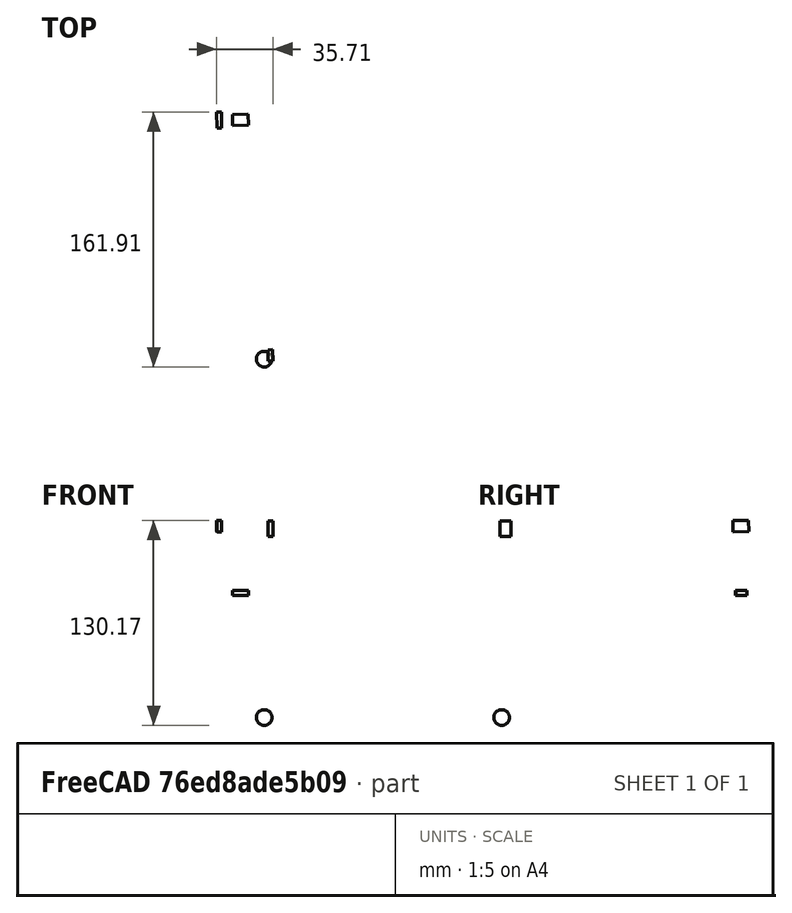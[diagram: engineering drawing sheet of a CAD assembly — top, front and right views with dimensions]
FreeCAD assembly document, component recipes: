
FREECAD ASSEMBLY — COMPONENT RECIPES ("3axis_robot_forced_reduced")

This assembly document has 3 components, labeled P0..P2 below (a component is one placed body or linked part). 3 of them carry a construction recipe — the FreeCAD feature program that regenerates the part from scratch, quoted from this document or its linked companion documents; the rest are supplied as boundary geometry only. No exploded tour is included for this assembly.
COMPONENT P0 — recipe-attached ("arm0", a linked part whose construction recipe lives in a companion FreeCAD document of the same project; that document's serialized recipe follows).
Construction recipe (the companion document, serialized — sketch geometry with constraints, then the solid features built on it; lengths are millimeters unless a unit is written):

FCSTD DOCUMENT  (FreeCAD 2024.1R35694 (Git))
Label: arm0
License: All rights reserved
LicenseURL: https://en.wikipedia.org/wiki/All_rights_reserved
objects: Sketcher::SketchObject×11, PartDesign::Pad×6, PartDesign::Hole×3, PartDesign::Body×2, PartDesign::Pocket×2, PartDesign::Fillet×1, App::Part×1
note: 37 computed .brp shape members not serialized (recipe doc carries the construction recipe); baked Part::Feature solids carry a one-line shape summary decoded from their .brp

FEATURE [Sketcher::SketchObject] Sketch
  FullyConstrained = true
  MapMode = 5
  Support = -> [XY_Plane001]
  sketch-geometry (5):
    g0: Circle CenterX=0 CenterY=0 CenterZ=0 NormalX=0 NormalY=0 NormalZ=1 AngleXU=0 Radius=2.5
    g1: ArcOfCircle CenterX=0 CenterY=0 CenterZ=0 NormalX=0 NormalY=0 NormalZ=1 AngleXU=0 Radius=7.5 StartAngle=1.5708 EndAngle=4.71239
    g2: LineSegment StartX=-1.2e-15 StartY=7.5 StartZ=0 EndX=15 EndY=7.5 EndZ=0
    g3: LineSegment StartX=15 StartY=7.5 StartZ=0 EndX=15 EndY=-7.5 EndZ=0
    g4: LineSegment StartX=15 StartY=-7.5 StartZ=0 EndX=1.8e-15 EndY=-7.5 EndZ=0
  constraints (12):
    c: Coincident(g0,g-1)
    c: Coincident(g1,g0)
    c: Diameter(g0) = 5
    c: Diameter(g1) = 15
    c: Horizontal(g2)
    c: Coincident(g2,g3)
    c: Vertical(g3)
    c: Coincident(g3,g4)
    c: Horizontal(g4)
    c: Tangent(g1,g4) = 1.5708
    c: Tangent(g1,g2) = 1.5708
    c: DistanceX(g2,g2) = 15
FEATURE [PartDesign::Pad] Pad
  Direction = (0,0,1)
  Length = 20
  Length2 = 10
  Profile = -> Sketch
  ReferenceAxis = -> Sketch [N_Axis]
  Refine = true
  Type = 0
FEATURE [Sketcher::SketchObject] Sketch001
  ExternalGeometry = -> [Pad]
  FullyConstrained = true
  MapMode = 5
  Placement = pos=(15,0,0) rot=(0.57735,0.57735,0.57735;2.0944rad)
  Support = -> [Pad]
  sketch-geometry (8):
    g0: LineSegment StartX=-7.5 StartY=0 StartZ=0 EndX=-21 EndY=43 EndZ=0
    g1: LineSegment StartX=-21 StartY=43 StartZ=0 EndX=-21 EndY=85 EndZ=0
    g2: LineSegment StartX=-21 StartY=85 StartZ=0 EndX=21 EndY=85 EndZ=0
    g3: LineSegment StartX=21 StartY=85 StartZ=0 EndX=21 EndY=43 EndZ=0
    g4: LineSegment StartX=21 StartY=43 StartZ=0 EndX=7.5 EndY=0 EndZ=0
    g5: LineSegment StartX=7.5 StartY=0 StartZ=0 EndX=-7.5 EndY=0 EndZ=0
    g6: GeomPoint X=5.2e-15 Y=64 Z=0
    g7: Circle CenterX=5.2e-15 CenterY=64 CenterZ=0 NormalX=0 NormalY=0 NormalZ=1 AngleXU=0 Radius=11.25
  constraints (18):
    c: PointOnObject(g0,g-1)
    c: Coincident(g0,g1)
    c: Vertical(g1)
    c: Coincident(g1,g2)
    c: Coincident(g2,g3)
    c: Coincident(g3,g4)
    c: Coincident(g4,g5)
    c: Coincident(g5,g0)
    c: Symmetric(g0,g3,g-2)
    c: Symmetric(g1,g2,g-2)
    c: DistanceX(g2,g2) = 42
    c: DistanceY(g3,g3) = 42
    c: Symmetric(g0,g4,g-2)
    c: DistanceX(g5,g5) = 15
    c: Symmetric(g1,g3,g6)
    c: Coincident(g7,g6)
    c: Diameter(g7) = 22.5
    c: DistanceY(g-1,g3) = 43
FEATURE [PartDesign::Pad] Pad001
  BaseFeature = -> Pad
  Direction = (1,0,0)
  Length = 4
  Length2 = 10
  Profile = -> Sketch001
  ReferenceAxis = -> Sketch001 [N_Axis]
  Refine = true
  Reversed = true
  Type = 0
FEATURE [Sketcher::SketchObject] Sketch003
  ExternalGeometry = -> [Pad001]
  FullyConstrained = true
  MapMode = 5
  Placement = pos=(11,0,0) rot=(0.57735,-0.57735,-0.57735;2.0944rad)
  Support = -> [Pad001]
  sketch-geometry (5):
    g0: Circle CenterX=15.5 CenterY=79.5 CenterZ=0 NormalX=0 NormalY=0 NormalZ=1 AngleXU=0 Radius=1.5
    g1: LineSegment StartX=-5.2e-15 StartY=64 StartZ=0 EndX=11.25 EndY=64 EndZ=0
    g2: Circle CenterX=-15.5 CenterY=79.5 CenterZ=0 NormalX=0 NormalY=0 NormalZ=1 AngleXU=0 Radius=1.5
    g3: Circle CenterX=15.5 CenterY=48.5 CenterZ=0 NormalX=0 NormalY=0 NormalZ=1 AngleXU=0 Radius=1.5
    g4: Circle CenterX=-15.5 CenterY=48.5 CenterZ=0 NormalX=0 NormalY=0 NormalZ=1 AngleXU=0 Radius=1.5
  constraints (12):
    c: DistanceY(g-3,g0) = 15.5
    c: DistanceX(g-3,g0) = 15.5
    c: Diameter(g0) = 3
    c: Coincident(g1,g-3)
    c: Horizontal(g1)
    c: PointOnObject(g1,g-3)
    c: Diameter(g2) = 3
    c: Diameter(g3) = 3
    c: Diameter(g4) = 3
    c: Symmetric(g2,g0,g-2)
    c: Symmetric(g4,g3,g-2)
    c: Symmetric(g3,g0,g1)
FEATURE [PartDesign::Hole] Hole
  BaseFeature = -> Pad001
  CustomThreadClearance = 0
  Depth = 25
  DepthType = 0
  Diameter = 3.4
  DrillForDepth = false
  DrillPoint = 1
  DrillPointAngle = 118
  HoleCutCountersinkAngle = 90
  HoleCutCustomValues = false
  HoleCutDepth = 2
  HoleCutDiameter = 6.1
  HoleCutType = 1
  ModelThread = false
  Profile = -> Sketch003
  Refine = true
  Tapered = false
  TaperedAngle = 90
  ThreadClass = 0
  ThreadDepth = 25
  ThreadDepthType = 0
  ThreadDirection = 0
  ThreadFit = 0
  ThreadSize = 9
  ThreadType = 1
  Threaded = false
  UseCustomThreadClearance = false
FEATURE [Sketcher::SketchObject] Sketch004
  ExternalGeometry = -> [Hole]
  FullyConstrained = true
  MapMode = 5
  Placement = pos=(0,0,20) rot=(0,0,1;0rad)
  Support = -> [Hole]
  sketch-geometry (1):
    g0: Circle CenterX=0 CenterY=0 CenterZ=0 NormalX=0 NormalY=0 NormalZ=1 AngleXU=0 Radius=2.5
  constraints (2):
    c: Coincident(g0,g-3)
    c: Equal(g0,g-3)
FEATURE [PartDesign::Pad] Pad002
  BaseFeature = -> Hole
  Direction = (0,0,1)
  Length = 2
  Length2 = 10
  Profile = -> Sketch004
  ReferenceAxis = -> Sketch004 [N_Axis]
  Refine = true
  Reversed = true
  Type = 0
FEATURE [PartDesign::Body] Body  label="arm0-skel"
  Group = -> [Sketch,Pad,Sketch001,Pad001,Sketch003,Hole,Sketch004,Pad002]
  Origin = -> Origin001
  Tip = -> Pad002
FEATURE [Sketcher::SketchObject] Sketch008
  FullyConstrained = true
  MapMode = 5
  Support = -> [XY_Plane002]
  sketch-geometry (5):
    g0: Circle CenterX=0 CenterY=0 CenterZ=0 NormalX=0 NormalY=0 NormalZ=1 AngleXU=0 Radius=2.5
    g1: ArcOfCircle CenterX=0 CenterY=0 CenterZ=0 NormalX=0 NormalY=0 NormalZ=1 AngleXU=0 Radius=7.5 StartAngle=1.5708 EndAngle=4.71239
    g2: LineSegment StartX=-1.2e-15 StartY=7.5 StartZ=0 EndX=15 EndY=7.5 EndZ=0
    g3: LineSegment StartX=15 StartY=7.5 StartZ=0 EndX=15 EndY=-7.5 EndZ=0
    g4: LineSegment StartX=15 StartY=-7.5 StartZ=0 EndX=1.8e-15 EndY=-7.5 EndZ=0
  constraints (12):
    c: Coincident(g0,g-1)
    c: Coincident(g1,g0)
    c: Diameter(g0) = 5
    c: Diameter(g1) = 15
    c: Horizontal(g2)
    c: Coincident(g2,g3)
    c: Vertical(g3)
    c: Coincident(g3,g4)
    c: Horizontal(g4)
    c: Tangent(g1,g4) = 1.5708
    c: Tangent(g1,g2) = 1.5708
    c: DistanceX(g2,g2) = 15
FEATURE [PartDesign::Pad] Pad003
  Direction = (0,0,1)
  Length = 20
  Length2 = 10
  Profile = -> Sketch008
  ReferenceAxis = -> Sketch008 [N_Axis]
  Refine = true
  Type = 0
FEATURE [Sketcher::SketchObject] Sketch009
  ExternalGeometry = -> [Pad003]
  FullyConstrained = true
  MapMode = 5
  Placement = pos=(15,0,0) rot=(0.57735,0.57735,0.57735;2.0944rad)
  Support = -> [Pad003]
  sketch-geometry (8):
    g0: LineSegment StartX=-7.5 StartY=0 StartZ=0 EndX=-21 EndY=43 EndZ=0
    g1: LineSegment StartX=-21 StartY=43 StartZ=0 EndX=-21 EndY=85 EndZ=0
    g2: LineSegment StartX=-21 StartY=85 StartZ=0 EndX=21 EndY=85 EndZ=0
    g3: LineSegment StartX=21 StartY=85 StartZ=0 EndX=21 EndY=43 EndZ=0
    g4: LineSegment StartX=21 StartY=43 StartZ=0 EndX=7.5 EndY=0 EndZ=0
    g5: LineSegment StartX=7.5 StartY=0 StartZ=0 EndX=-7.5 EndY=0 EndZ=0
    g6: GeomPoint X=4.8e-15 Y=64 Z=0
    g7: Circle CenterX=4.8e-15 CenterY=64 CenterZ=0 NormalX=0 NormalY=0 NormalZ=1 AngleXU=0 Radius=11.25
  constraints (18):
    c: PointOnObject(g0,g-1)
    c: Coincident(g0,g1)
    c: Vertical(g1)
    c: Coincident(g1,g2)
    c: Coincident(g2,g3)
    c: Coincident(g3,g4)
    c: Coincident(g4,g5)
    c: Coincident(g5,g0)
    c: Symmetric(g0,g3,g-2)
    c: Symmetric(g1,g2,g-2)
    c: DistanceX(g2,g2) = 42
    c: DistanceY(g3,g3) = 42
    c: Symmetric(g0,g4,g-2)
    c: DistanceX(g5,g5) = 15
    c: Symmetric(g1,g3,g6)
    c: Coincident(g7,g6)
    c: Diameter(g7) = 22.5
    c: DistanceY(g-1,g3) = 43
FEATURE [PartDesign::Pad] Pad004
  BaseFeature = -> Pad003
  Direction = (1,0,0)
  Length = 4
  Length2 = 10
  Profile = -> Sketch009
  ReferenceAxis = -> Sketch009 [N_Axis]
  Refine = true
  Reversed = true
  Type = 0
FEATURE [Sketcher::SketchObject] Sketch010
  ExternalGeometry = -> [Pad004]
  FullyConstrained = true
  MapMode = 5
  Placement = pos=(11,0,0) rot=(0.57735,-0.57735,-0.57735;2.0944rad)
  Support = -> [Pad004]
  sketch-geometry (5):
    g0: Circle CenterX=15.5 CenterY=79.5 CenterZ=0 NormalX=0 NormalY=0 NormalZ=1 AngleXU=0 Radius=1.5
    g1: LineSegment StartX=-4.8e-15 StartY=64 StartZ=0 EndX=11.25 EndY=64 EndZ=0
    g2: Circle CenterX=-15.5 CenterY=79.5 CenterZ=0 NormalX=0 NormalY=0 NormalZ=1 AngleXU=0 Radius=1.5
    g3: Circle CenterX=15.5 CenterY=48.5 CenterZ=0 NormalX=0 NormalY=0 NormalZ=1 AngleXU=0 Radius=1.5
    g4: Circle CenterX=-15.5 CenterY=48.5 CenterZ=0 NormalX=0 NormalY=0 NormalZ=1 AngleXU=0 Radius=1.5
  constraints (12):
    c: DistanceY(g-3,g0) = 15.5
    c: DistanceX(g-3,g0) = 15.5
    c: Diameter(g0) = 3
    c: Coincident(g1,g-3)
    c: Horizontal(g1)
    c: PointOnObject(g1,g-3)
    c: Diameter(g2) = 3
    c: Diameter(g3) = 3
    c: Diameter(g4) = 3
    c: Symmetric(g2,g0,g-2)
    c: Symmetric(g4,g3,g-2)
    c: Symmetric(g3,g0,g1)
FEATURE [PartDesign::Hole] Hole002
  BaseFeature = -> Pad004
  CustomThreadClearance = 0
  Depth = 25
  DepthType = 0
  Diameter = 3.4
  DrillForDepth = false
  DrillPoint = 1
  DrillPointAngle = 118
  HoleCutCountersinkAngle = 90
  HoleCutCustomValues = false
  HoleCutDepth = 2
  HoleCutDiameter = 6.1
  HoleCutType = 1
  ModelThread = false
  Profile = -> Sketch010
  Refine = true
  Tapered = false
  TaperedAngle = 90
  ThreadClass = 0
  ThreadDepth = 25
  ThreadDepthType = 0
  ThreadDirection = 0
  ThreadFit = 0
  ThreadSize = 9
  ThreadType = 1
  Threaded = false
  UseCustomThreadClearance = false
FEATURE [Sketcher::SketchObject] Sketch011
  ExternalGeometry = -> [Hole002]
  FullyConstrained = true
  MapMode = 5
  Placement = pos=(0,0,20) rot=(0,0,1;0rad)
  Support = -> [Hole002]
  sketch-geometry (1):
    g0: Circle CenterX=0 CenterY=0 CenterZ=0 NormalX=0 NormalY=0 NormalZ=1 AngleXU=0 Radius=2.5
  constraints (2):
    c: Coincident(g0,g-3)
    c: Equal(g0,g-3)
FEATURE [PartDesign::Pad] Pad005
  BaseFeature = -> Hole002
  Direction = (0,0,1)
  Length = 2
  Length2 = 10
  Profile = -> Sketch011
  ReferenceAxis = -> Sketch011 [N_Axis]
  Refine = true
  Reversed = true
  Type = 0
FEATURE [Sketcher::SketchObject] Sketch012
  FullyConstrained = true
  MapMode = 5
  Placement = pos=(0,0,0) rot=(1,0,0;3.14159rad)
  Support = -> [Pad005]
  sketch-geometry (4):
    g0: LineSegment StartX=0 StartY=1 StartZ=0 EndX=0 EndY=-1 EndZ=0
    g1: LineSegment StartX=0 StartY=-1 StartZ=0 EndX=10 EndY=-1 EndZ=0
    g2: LineSegment StartX=10 StartY=-1 StartZ=0 EndX=10 EndY=1 EndZ=0
    g3: LineSegment StartX=10 StartY=1 StartZ=0 EndX=0 EndY=1 EndZ=0
  constraints (11):
    c: Coincident(g0,g1)
    c: Coincident(g1,g2)
    c: Coincident(g2,g3)
    c: Coincident(g3,g0)
    c: Vertical(g0)
    c: Horizontal(g1)
    c: Horizontal(g3)
    c: PointOnObject(g0,g-2)
    c: Symmetric(g1,g2,g-1)
    c: DistanceY(g2,g2) = 2
    c: DistanceX(g3,g3) = 10
FEATURE [PartDesign::Pocket] Pocket002
  BaseFeature = -> Pad005
  Direction = (0,0,1)
  Length = 5
  Length2 = 5
  Profile = -> Sketch012
  ReferenceAxis = -> Sketch012 [N_Axis]
  Refine = true
  Type = 1
FEATURE [Sketcher::SketchObject] Sketch013
  FullyConstrained = true
  MapMode = 5
  Placement = pos=(0,-7.5,0) rot=(1,0,0;1.5708rad)
  Support = -> [Pocket002]
  sketch-geometry (1):
    g0: Circle CenterX=6 CenterY=10 CenterZ=0 NormalX=0 NormalY=0 NormalZ=1 AngleXU=0 Radius=1.5
  constraints (3):
    c: DistanceY(g-1,g0) = 10
    c: DistanceX(g-1,g0) = 6
    c: Diameter(g0) = 3
FEATURE [PartDesign::Hole] Hole003
  BaseFeature = -> Pocket002
  CustomThreadClearance = 0
  Depth = 25
  DepthType = 0
  Diameter = 4.5
  DrillForDepth = false
  DrillPoint = 1
  DrillPointAngle = 118
  HoleCutCountersinkAngle = 90
  HoleCutCustomValues = false
  HoleCutDepth = 0
  HoleCutDiameter = 6.1
  HoleCutType = 0
  ModelThread = false
  Profile = -> Sketch013
  Refine = true
  Tapered = false
  TaperedAngle = 90
  ThreadClass = 0
  ThreadDepth = 25
  ThreadDepthType = 0
  ThreadDirection = 0
  ThreadFit = 0
  ThreadSize = 11
  ThreadType = 1
  Threaded = false
  UseCustomThreadClearance = false
FEATURE [Sketcher::SketchObject] Sketch014
  ExternalGeometry = -> [Hole003]
  FullyConstrained = true
  MapMode = 5
  Placement = pos=(0,7.5,0) rot=(0,0.707107,0.707107;3.14159rad)
  Support = -> [Hole003]
  sketch-geometry (7):
    g0: LineSegment StartX=-1.95855 StartY=10 StartZ=0 EndX=-3.97927 EndY=13.5 EndZ=0
    g1: LineSegment StartX=-3.97927 StartY=13.5 StartZ=0 EndX=-8.02073 EndY=13.5 EndZ=0
    g2: LineSegment StartX=-8.02073 StartY=13.5 StartZ=0 EndX=-10.0415 EndY=10 EndZ=0
    g3: LineSegment StartX=-10.0415 StartY=10 StartZ=0 EndX=-8.02073 EndY=6.5 EndZ=0
    g4: LineSegment StartX=-8.02073 StartY=6.5 StartZ=0 EndX=-3.97927 EndY=6.5 EndZ=0
    g5: LineSegment StartX=-3.97927 StartY=6.5 StartZ=0 EndX=-1.95855 EndY=10 EndZ=0
    g6: Circle CenterX=-6 CenterY=10 CenterZ=0 NormalX=0 NormalY=0 NormalZ=1 AngleXU=0 Radius=4.04145
  constraints (16):
    c: Coincident(g0,g1)
    c: Coincident(g1,g2)
    c: Coincident(g2,g3)
    c: Coincident(g3,g4)
    c: Coincident(g4,g5)
    c: Coincident(g5,g0)
    c: Equal(g0, g1-g5) x5
    c: PointOnObject(g0,g6)
    c: PointOnObject(g1,g6)
    c: PointOnObject(g2,g6)
    c: PointOnObject(g3,g6)
    c: PointOnObject(g4,g6)
    c: PointOnObject(g5,g6)
    c: Coincident(g6,g-3)
    c: Horizontal(g1)
    c: DistanceY(g4,g0) = 7
FEATURE [PartDesign::Pocket] Pocket003
  BaseFeature = -> Hole003
  Direction = (0,-1,2e-16)
  Length = 4
  Length2 = 5
  Profile = -> Sketch014
  ReferenceAxis = -> Sketch014 [N_Axis]
  Refine = true
  Type = 0
FEATURE [PartDesign::Fillet] Fillet
  Base = -> Pocket003 [Edge77,Edge78,Edge65,Edge54]
  BaseFeature = -> Pocket003
  Radius = 6
  Refine = true
  SupportTransform = false
  UseAllEdges = false
FEATURE [PartDesign::Body] Body001  label="arm0s"
  Group = -> [Sketch008,Pad003,Sketch009,Pad004,Sketch010,Hole002,Sketch011,Pad005,Sketch012,Pocket002,Sketch013,Hole003,Sketch014,Pocket003,Fillet]
  Origin = -> Origin002
  Tip = -> Fillet
FEATURE [App::Part] Part  label="arm0"
  Group = -> [Body,Body001]
  Origin = -> Origin
COMPONENT P1 — recipe-attached ("arm1", a linked part whose construction recipe lives in a companion FreeCAD document of the same project; that document's serialized recipe follows).
Construction recipe (the companion document, serialized — sketch geometry with constraints, then the solid features built on it; lengths are millimeters unless a unit is written):

FCSTD DOCUMENT  (FreeCAD 2024.1R35694 (Git))
Label: arm1
License: All rights reserved
LicenseURL: https://en.wikipedia.org/wiki/All_rights_reserved
objects: Sketcher::SketchObject×17, PartDesign::Pad×11, PartDesign::Chamfer×8, PartDesign::Plane×4, PartDesign::Hole×3, PartDesign::Pocket×3, PartDesign::Body×2, PartDesign::Fillet×1, App::Part×1
note: 75 computed .brp shape members not serialized (recipe doc carries the construction recipe); baked Part::Feature solids carry a one-line shape summary decoded from their .brp

FEATURE [Sketcher::SketchObject] Sketch
  FullyConstrained = true
  MapMode = 5
  Support = -> [XY_Plane001]
  sketch-geometry (5):
    g0: Circle CenterX=0 CenterY=0 CenterZ=0 NormalX=0 NormalY=0 NormalZ=1 AngleXU=0 Radius=2.5
    g1: ArcOfCircle CenterX=0 CenterY=0 CenterZ=0 NormalX=0 NormalY=0 NormalZ=1 AngleXU=0 Radius=7.5 StartAngle=1.5708 EndAngle=4.71239
    g2: LineSegment StartX=-1.2e-15 StartY=7.5 StartZ=0 EndX=15 EndY=7.5 EndZ=0
    g3: LineSegment StartX=15 StartY=7.5 StartZ=0 EndX=15 EndY=-7.5 EndZ=0
    g4: LineSegment StartX=15 StartY=-7.5 StartZ=0 EndX=1.8e-15 EndY=-7.5 EndZ=0
  constraints (12):
    c: Coincident(g0,g-1)
    c: Coincident(g1,g0)
    c: Diameter(g0) = 5
    c: Diameter(g1) = 15
    c: Horizontal(g2)
    c: Coincident(g2,g3)
    c: Vertical(g3)
    c: Coincident(g3,g4)
    c: Horizontal(g4)
    c: Tangent(g1,g4) = 1.5708
    c: Tangent(g1,g2) = 1.5708
    c: DistanceX(g2,g2) = 15
FEATURE [PartDesign::Pad] Pad
  Direction = (0,0,1)
  Length = 20
  Length2 = 10
  Profile = -> Sketch
  ReferenceAxis = -> Sketch [N_Axis]
  Refine = true
  Type = 0
FEATURE [Sketcher::SketchObject] Sketch001
  ExternalGeometry = -> [Pad]
  FullyConstrained = true
  MapMode = 5
  Placement = pos=(15,0,0) rot=(0.57735,0.57735,0.57735;2.0944rad)
  Support = -> [Pad]
  sketch-geometry (8):
    g0: LineSegment StartX=-7.5 StartY=0 StartZ=0 EndX=-21 EndY=11 EndZ=0
    g1: LineSegment StartX=-21 StartY=11 StartZ=0 EndX=-21 EndY=53 EndZ=0
    g2: LineSegment StartX=-21 StartY=53 StartZ=0 EndX=21 EndY=53 EndZ=0
    g3: LineSegment StartX=21 StartY=53 StartZ=0 EndX=21 EndY=11 EndZ=0
    g4: LineSegment StartX=21 StartY=11 StartZ=0 EndX=7.5 EndY=0 EndZ=0
    g5: LineSegment StartX=7.5 StartY=0 StartZ=0 EndX=-7.5 EndY=0 EndZ=0
    g6: GeomPoint X=-1.2e-15 Y=32 Z=0
    g7: Circle CenterX=-1.2e-15 CenterY=32 CenterZ=0 NormalX=0 NormalY=0 NormalZ=1 AngleXU=0 Radius=11.25
  constraints (18):
    c: PointOnObject(g0,g-1)
    c: Coincident(g0,g1)
    c: Vertical(g1)
    c: Coincident(g1,g2)
    c: Coincident(g2,g3)
    c: Coincident(g3,g4)
    c: Coincident(g4,g5)
    c: Coincident(g5,g0)
    c: Symmetric(g0,g3,g-2)
    c: Symmetric(g1,g2,g-2)
    c: DistanceX(g2,g2) = 42
    c: DistanceY(g3,g3) = 42
    c: Symmetric(g0,g4,g-2)
    c: DistanceX(g5,g5) = 15
    c: Symmetric(g1,g3,g6)
    c: Coincident(g7,g6)
    c: Diameter(g7) = 22.5
    c: DistanceY(g-1,g3) = 11
FEATURE [PartDesign::Pad] Pad001
  BaseFeature = -> Pad
  Direction = (1,0,0)
  Length = 4
  Length2 = 10
  Profile = -> Sketch001
  ReferenceAxis = -> Sketch001 [N_Axis]
  Refine = true
  Reversed = true
  Type = 0
FEATURE [Sketcher::SketchObject] Sketch003
  ExternalGeometry = -> [Pad001]
  FullyConstrained = true
  MapMode = 5
  Placement = pos=(11,0,0) rot=(0.57735,-0.57735,-0.57735;2.0944rad)
  Support = -> [Pad001]
  sketch-geometry (5):
    g0: Circle CenterX=15.5 CenterY=47.5 CenterZ=0 NormalX=0 NormalY=0 NormalZ=1 AngleXU=0 Radius=1.5
    g1: LineSegment StartX=1.2e-15 StartY=32 StartZ=0 EndX=11.25 EndY=32 EndZ=0
    g2: Circle CenterX=-15.5 CenterY=47.5 CenterZ=0 NormalX=0 NormalY=0 NormalZ=1 AngleXU=0 Radius=1.5
    g3: Circle CenterX=15.5 CenterY=16.5 CenterZ=0 NormalX=0 NormalY=0 NormalZ=1 AngleXU=0 Radius=1.5
    g4: Circle CenterX=-15.5 CenterY=16.5 CenterZ=0 NormalX=0 NormalY=0 NormalZ=1 AngleXU=0 Radius=1.5
  constraints (12):
    c: DistanceY(g-3,g0) = 15.5
    c: DistanceX(g-3,g0) = 15.5
    c: Diameter(g0) = 3
    c: Coincident(g1,g-3)
    c: Horizontal(g1)
    c: PointOnObject(g1,g-3)
    c: Diameter(g2) = 3
    c: Diameter(g3) = 3
    c: Diameter(g4) = 3
    c: Symmetric(g2,g0,g-2)
    c: Symmetric(g4,g3,g-2)
    c: Symmetric(g3,g0,g1)
FEATURE [PartDesign::Hole] Hole
  BaseFeature = -> Pad001
  CustomThreadClearance = 0
  Depth = 25
  DepthType = 0
  Diameter = 3.4
  DrillForDepth = false
  DrillPoint = 1
  DrillPointAngle = 118
  HoleCutCountersinkAngle = 90
  HoleCutCustomValues = false
  HoleCutDepth = 2
  HoleCutDiameter = 6.1
  HoleCutType = 1
  ModelThread = false
  Profile = -> Sketch003
  Refine = true
  Tapered = false
  TaperedAngle = 90
  ThreadClass = 0
  ThreadDepth = 25
  ThreadDepthType = 0
  ThreadDirection = 0
  ThreadFit = 0
  ThreadSize = 9
  ThreadType = 1
  Threaded = false
  UseCustomThreadClearance = false
FEATURE [Sketcher::SketchObject] Sketch004
  ExternalGeometry = -> [Hole]
  FullyConstrained = true
  MapMode = 5
  Placement = pos=(0,0,20) rot=(0,0,1;0rad)
  Support = -> [Hole]
  sketch-geometry (1):
    g0: Circle CenterX=0 CenterY=0 CenterZ=0 NormalX=0 NormalY=0 NormalZ=1 AngleXU=0 Radius=2.5
  constraints (2):
    c: Coincident(g0,g-3)
    c: Equal(g0,g-3)
FEATURE [PartDesign::Pad] Pad002
  BaseFeature = -> Hole
  Direction = (0,0,1)
  Length = 2
  Length2 = 10
  Profile = -> Sketch004
  ReferenceAxis = -> Sketch004 [N_Axis]
  Refine = true
  Reversed = true
  Type = 0
FEATURE [Sketcher::SketchObject] Sketch005
  FullyConstrained = true
  MapMode = 5
  Placement = pos=(0,0,0) rot=(1,0,0;3.14159rad)
  Support = -> [Pad002]
  sketch-geometry (4):
    g0: LineSegment StartX=0 StartY=1 StartZ=0 EndX=0 EndY=-1 EndZ=0
    g1: LineSegment StartX=0 StartY=-1 StartZ=0 EndX=10 EndY=-1 EndZ=0
    g2: LineSegment StartX=10 StartY=-1 StartZ=0 EndX=10 EndY=1 EndZ=0
    g3: LineSegment StartX=10 StartY=1 StartZ=0 EndX=0 EndY=1 EndZ=0
  constraints (11):
    c: Coincident(g0,g1)
    c: Coincident(g1,g2)
    c: Coincident(g2,g3)
    c: Coincident(g3,g0)
    c: Vertical(g0)
    c: Horizontal(g1)
    c: Horizontal(g3)
    c: PointOnObject(g0,g-2)
    c: Symmetric(g1,g2,g-1)
    c: DistanceY(g2,g2) = 2
    c: DistanceX(g3,g3) = 10
FEATURE [PartDesign::Pocket] Pocket
  BaseFeature = -> Pad002
  Direction = (0,0,1)
  Length = 5
  Length2 = 5
  Profile = -> Sketch005
  ReferenceAxis = -> Sketch005 [N_Axis]
  Refine = true
  Type = 1
FEATURE [Sketcher::SketchObject] Sketch006
  FullyConstrained = true
  MapMode = 5
  Placement = pos=(0,-7.5,0) rot=(1,0,0;1.5708rad)
  Support = -> [Pocket]
  sketch-geometry (1):
    g0: Circle CenterX=6 CenterY=10 CenterZ=0 NormalX=0 NormalY=0 NormalZ=1 AngleXU=0 Radius=1.5
  constraints (3):
    c: DistanceY(g-1,g0) = 10
    c: DistanceX(g-1,g0) = 6
    c: Diameter(g0) = 3
FEATURE [PartDesign::Hole] Hole001
  BaseFeature = -> Pocket
  CustomThreadClearance = 0
  Depth = 25
  DepthType = 0
  Diameter = 4.5
  DrillForDepth = false
  DrillPoint = 1
  DrillPointAngle = 118
  HoleCutCountersinkAngle = 90
  HoleCutCustomValues = false
  HoleCutDepth = 0
  HoleCutDiameter = 6.1
  HoleCutType = 0
  ModelThread = false
  Profile = -> Sketch006
  Refine = true
  Tapered = false
  TaperedAngle = 90
  ThreadClass = 0
  ThreadDepth = 25
  ThreadDepthType = 0
  ThreadDirection = 0
  ThreadFit = 0
  ThreadSize = 11
  ThreadType = 1
  Threaded = false
  UseCustomThreadClearance = false
FEATURE [Sketcher::SketchObject] Sketch007
  ExternalGeometry = -> [Hole001]
  FullyConstrained = true
  MapMode = 5
  Placement = pos=(0,7.5,0) rot=(0,0.707107,0.707107;3.14159rad)
  Support = -> [Hole001]
  sketch-geometry (7):
    g0: LineSegment StartX=-6 StartY=14.0415 StartZ=0 EndX=-9.5 EndY=12.0207 EndZ=0
    g1: LineSegment StartX=-9.5 StartY=12.0207 StartZ=0 EndX=-9.5 EndY=7.97927 EndZ=0
    g2: LineSegment StartX=-9.5 StartY=7.97927 StartZ=0 EndX=-6 EndY=5.95855 EndZ=0
    g3: LineSegment StartX=-6 StartY=5.95855 StartZ=0 EndX=-2.5 EndY=7.97927 EndZ=0
    g4: LineSegment StartX=-2.5 StartY=7.97927 StartZ=0 EndX=-2.5 EndY=12.0207 EndZ=0
    g5: LineSegment StartX=-2.5 StartY=12.0207 StartZ=0 EndX=-6 EndY=14.0415 EndZ=0
    g6: Circle CenterX=-6 CenterY=10 CenterZ=0 NormalX=0 NormalY=0 NormalZ=1 AngleXU=0 Radius=4.04145
  constraints (16):
    c: Coincident(g0,g1)
    c: Coincident(g1,g2)
    c: Coincident(g2,g3)
    c: Coincident(g3,g4)
    c: Coincident(g4,g5)
    c: Coincident(g5,g0)
    c: Equal(g0, g1-g5) x5
    c: PointOnObject(g0,g6)
    c: PointOnObject(g1,g6)
    c: PointOnObject(g2,g6)
    c: PointOnObject(g3,g6)
    c: PointOnObject(g4,g6)
    c: PointOnObject(g5,g6)
    c: Coincident(g6,g-3)
    c: Vertical(g4)
    c: DistanceX(g0,g4) = 7
FEATURE [PartDesign::Pocket] Pocket001
  BaseFeature = -> Hole001
  Direction = (0,-1,2e-16)
  Length = 4
  Length2 = 5
  Profile = -> Sketch007
  ReferenceAxis = -> Sketch007 [N_Axis]
  Refine = true
  Type = 0
FEATURE [Sketcher::SketchObject] Sketch008
  ExternalGeometry = -> [Pocket001]
  FullyConstrained = true
  MapMode = 5
  Placement = pos=(0,0,0) rot=(1,0,0;3.14159rad)
  Support = -> [Pocket001]
  sketch-geometry (5):
    g0: Circle CenterX=-150 CenterY=2.37e-14 CenterZ=0 NormalX=0 NormalY=0 NormalZ=1 AngleXU=0 Radius=8
    g1: ArcOfCircle CenterX=-150 CenterY=2.37e-14 CenterZ=0 NormalX=0 NormalY=0 NormalZ=1 AngleXU=0 Radius=11 StartAngle=0.276227 EndAngle=6.00696
    g2: ArcOfCircle CenterX=0 CenterY=0 CenterZ=0 NormalX=0 NormalY=0 NormalZ=1 AngleXU=0 Radius=7.5 StartAngle=2.73008 EndAngle=3.55311
    g3: LineSegment StartX=-139.417 StartY=3 StartZ=0 EndX=-6.87386 EndY=3 EndZ=0
    g4: LineSegment StartX=-139.417 StartY=-3 StartZ=0 EndX=-6.87386 EndY=-3 EndZ=0
  constraints (14):
    c: Coincident(g1,g0)
    c: Equal(g2,g-3)
    c: Horizontal(g3)
    c: Horizontal(g4)
    c: Coincident(g1,g4)
    c: Coincident(g1,g3)
    c: Coincident(g2,g3)
    c: Coincident(g2,g4)
    c: Symmetric(g1,g1,g-1)
    c: Distance(g1,g1) = 6
    c: Diameter(g0) = 16
    c: Diameter(g1) = 22
    c: DistanceX(g0,g-1) = 150
    c: Coincident(g2,g-3)
FEATURE [PartDesign::Pad] Pad003
  BaseFeature = -> Pocket001
  Direction = (0,0,-1)
  Length = 10
  Length2 = 10
  Profile = -> Sketch008
  ReferenceAxis = -> Sketch008 [N_Axis]
  Refine = true
  Reversed = true
  Type = 0
FEATURE [PartDesign::Plane] DatumPlane
  AttachmentOffset = pos=(0,0,-145) rot=(0,0,1;0rad)
  Length = 62.49
  MapMode = 5
  Placement = pos=(-130,0,0) rot=(0.57735,0.57735,0.57735;2.0944rad)
  ResizeMode = 0
  Support = -> [Pad003]
  Width = 90.49
FEATURE [Sketcher::SketchObject] Sketch009
  ExternalGeometry = -> [Pad003]
  FullyConstrained = true
  MapMode = 5
  Placement = pos=(-130,0,0) rot=(0.57735,0.57735,0.57735;2.0944rad)
  Support = -> [DatumPlane]
  sketch-geometry (5):
    g0: Circle CenterX=-1.2e-15 CenterY=32 CenterZ=0 NormalX=0 NormalY=0 NormalZ=1 AngleXU=0 Radius=8
    g1: ArcOfCircle CenterX=-1.2e-15 CenterY=32 CenterZ=0 NormalX=0 NormalY=0 NormalZ=1 AngleXU=0 Radius=11 StartAngle=4.98862 EndAngle=10.7193
    g2: LineSegment StartX=3 StartY=10 StartZ=0 EndX=-3 EndY=10 EndZ=0
    g3: LineSegment StartX=-3 StartY=10 StartZ=0 EndX=-3 EndY=21.417 EndZ=0
    g4: LineSegment StartX=3 StartY=10 StartZ=0 EndX=3 EndY=21.417 EndZ=0
  constraints (12):
    c: Coincident(g0,g-6)
    c: Coincident(g1,g0)
    c: Diameter(g0) = 16
    c: Diameter(g1) = 22
    c: Coincident(g2,g-4)
    c: Coincident(g2,g-5)
    c: Coincident(g2,g3)
    c: Coincident(g2,g4)
    c: Vertical(g4)
    c: Vertical(g3)
    c: Coincident(g1,g3)
    c: Coincident(g1,g4)
FEATURE [PartDesign::Pad] Pad004
  BaseFeature = -> Pad003
  Direction = (1,0,0)
  Length = 5
  Length2 = 10
  Profile = -> Sketch009
  ReferenceAxis = -> Sketch009 [N_Axis]
  Refine = true
  Type = 0
FEATURE [Sketcher::SketchObject] Sketch010
  FullyConstrained = true
  MapMode = 5
  Support = -> [XY_Plane002]
  sketch-geometry (5):
    g0: Circle CenterX=0 CenterY=0 CenterZ=0 NormalX=0 NormalY=0 NormalZ=1 AngleXU=0 Radius=2.5
    g1: ArcOfCircle CenterX=0 CenterY=0 CenterZ=0 NormalX=0 NormalY=0 NormalZ=1 AngleXU=0 Radius=7.5 StartAngle=1.5708 EndAngle=4.71239
    g2: LineSegment StartX=-1.2e-15 StartY=7.5 StartZ=0 EndX=15 EndY=7.5 EndZ=0
    g3: LineSegment StartX=15 StartY=7.5 StartZ=0 EndX=15 EndY=-7.5 EndZ=0
    g4: LineSegment StartX=15 StartY=-7.5 StartZ=0 EndX=1.8e-15 EndY=-7.5 EndZ=0
  constraints (12):
    c: Coincident(g0,g-1)
    c: Coincident(g1,g0)
    c: Diameter(g0) = 5
    c: Diameter(g1) = 15
    c: Horizontal(g2)
    c: Coincident(g2,g3)
    c: Vertical(g3)
    c: Coincident(g3,g4)
    c: Horizontal(g4)
    c: Tangent(g1,g4) = 1.5708
    c: Tangent(g1,g2) = 1.5708
    c: DistanceX(g2,g2) = 15
FEATURE [PartDesign::Pad] Pad005
  Direction = (0,0,1)
  Length = 20
  Length2 = 10
  Profile = -> Sketch010
  ReferenceAxis = -> Sketch010 [N_Axis]
  Refine = true
  Type = 0
FEATURE [Sketcher::SketchObject] Sketch011
  ExternalGeometry = -> [Pad005]
  FullyConstrained = true
  MapMode = 5
  Placement = pos=(15,0,0) rot=(0.57735,0.57735,0.57735;2.0944rad)
  Support = -> [Pad005]
  sketch-geometry (8):
    g0: LineSegment StartX=-7.5 StartY=0 StartZ=0 EndX=-21 EndY=11 EndZ=0
    g1: LineSegment StartX=-21 StartY=11 StartZ=0 EndX=-21 EndY=53 EndZ=0
    g2: LineSegment StartX=-21 StartY=53 StartZ=0 EndX=21 EndY=53 EndZ=0
    g3: LineSegment StartX=21 StartY=53 StartZ=0 EndX=21 EndY=11 EndZ=0
    g4: LineSegment StartX=21 StartY=11 StartZ=0 EndX=7.5 EndY=0 EndZ=0
    g5: LineSegment StartX=7.5 StartY=0 StartZ=0 EndX=-7.5 EndY=0 EndZ=0
    g6: GeomPoint X=-1.2e-15 Y=32 Z=0
    g7: Circle CenterX=-1.2e-15 CenterY=32 CenterZ=0 NormalX=0 NormalY=0 NormalZ=1 AngleXU=0 Radius=11.25
  constraints (18):
    c: PointOnObject(g0,g-1)
    c: Coincident(g0,g1)
    c: Vertical(g1)
    c: Coincident(g1,g2)
    c: Coincident(g2,g3)
    c: Coincident(g3,g4)
    c: Coincident(g4,g5)
    c: Coincident(g5,g0)
    c: Symmetric(g0,g3,g-2)
    c: Symmetric(g1,g2,g-2)
    c: DistanceX(g2,g2) = 42
    c: DistanceY(g3,g3) = 42
    c: Symmetric(g0,g4,g-2)
    c: DistanceX(g5,g5) = 15
    c: Symmetric(g1,g3,g6)
    c: Coincident(g7,g6)
    c: Diameter(g7) = 22.5
    c: DistanceY(g-1,g3) = 11
FEATURE [PartDesign::Pad] Pad006
  BaseFeature = -> Pad005
  Direction = (1,0,0)
  Length = 4
  Length2 = 10
  Profile = -> Sketch011
  ReferenceAxis = -> Sketch011 [N_Axis]
  Refine = true
  Reversed = true
  Type = 0
FEATURE [Sketcher::SketchObject] Sketch012
  ExternalGeometry = -> [Pad006]
  FullyConstrained = true
  MapMode = 5
  Placement = pos=(11,0,0) rot=(0.57735,-0.57735,-0.57735;2.0944rad)
  Support = -> [Pad006]
  sketch-geometry (5):
    g0: Circle CenterX=15.5 CenterY=47.5 CenterZ=0 NormalX=0 NormalY=0 NormalZ=1 AngleXU=0 Radius=1.5
    g1: LineSegment StartX=1.2e-15 StartY=32 StartZ=0 EndX=11.25 EndY=32 EndZ=0
    g2: Circle CenterX=-15.5 CenterY=47.5 CenterZ=0 NormalX=0 NormalY=0 NormalZ=1 AngleXU=0 Radius=1.5
    g3: Circle CenterX=15.5 CenterY=16.5 CenterZ=0 NormalX=0 NormalY=0 NormalZ=1 AngleXU=0 Radius=1.5
    g4: Circle CenterX=-15.5 CenterY=16.5 CenterZ=0 NormalX=0 NormalY=0 NormalZ=1 AngleXU=0 Radius=1.5
  constraints (12):
    c: DistanceY(g-3,g0) = 15.5
    c: DistanceX(g-3,g0) = 15.5
    c: Diameter(g0) = 3
    c: Coincident(g1,g-3)
    c: Horizontal(g1)
    c: PointOnObject(g1,g-3)
    c: Diameter(g2) = 3
    c: Diameter(g3) = 3
    c: Diameter(g4) = 3
    c: Symmetric(g2,g0,g-2)
    c: Symmetric(g4,g3,g-2)
    c: Symmetric(g3,g0,g1)
FEATURE [PartDesign::Hole] Hole002
  BaseFeature = -> Pad006
  CustomThreadClearance = 0
  Depth = 25
  DepthType = 0
  Diameter = 3.4
  DrillForDepth = false
  DrillPoint = 1
  DrillPointAngle = 118
  HoleCutCountersinkAngle = 90
  HoleCutCustomValues = false
  HoleCutDepth = 2
  HoleCutDiameter = 6.1
  HoleCutType = 1
  ModelThread = false
  Profile = -> Sketch012
  Refine = true
  Tapered = false
  TaperedAngle = 90
  ThreadClass = 0
  ThreadDepth = 25
  ThreadDepthType = 0
  ThreadDirection = 0
  ThreadFit = 0
  ThreadSize = 9
  ThreadType = 1
  Threaded = false
  UseCustomThreadClearance = false
FEATURE [Sketcher::SketchObject] Sketch013
  ExternalGeometry = -> [Hole002]
  FullyConstrained = true
  MapMode = 5
  Placement = pos=(0,0,20) rot=(0,0,1;0rad)
  Support = -> [Hole002]
  sketch-geometry (1):
    g0: Circle CenterX=0 CenterY=0 CenterZ=0 NormalX=0 NormalY=0 NormalZ=1 AngleXU=0 Radius=2.5
  constraints (2):
    c: Coincident(g0,g-3)
    c: Equal(g0,g-3)
FEATURE [PartDesign::Pad] Pad007
  BaseFeature = -> Hole002
  Direction = (0,0,1)
  Length = 2
  Length2 = 10
  Profile = -> Sketch013
  ReferenceAxis = -> Sketch013 [N_Axis]
  Refine = true
  Reversed = true
  Type = 0
FEATURE [Sketcher::SketchObject] Sketch017
  ExternalGeometry = -> [Pad007]
  FullyConstrained = true
  MapMode = 5
  Placement = pos=(0,0,0) rot=(1,0,0;3.14159rad)
  sketch-geometry (5):
    g0: Circle CenterX=-150 CenterY=4.1e-15 CenterZ=0 NormalX=0 NormalY=0 NormalZ=1 AngleXU=0 Radius=8
    g1: ArcOfCircle CenterX=-150 CenterY=4.1e-15 CenterZ=0 NormalX=0 NormalY=0 NormalZ=1 AngleXU=0 Radius=11 StartAngle=0.276227 EndAngle=6.00696
    g2: ArcOfCircle CenterX=7.9e-15 CenterY=2e-14 CenterZ=0 NormalX=0 NormalY=0 NormalZ=1 AngleXU=0 Radius=7.5 StartAngle=2.73008 EndAngle=3.55311
    g3: LineSegment StartX=-139.417 StartY=3 StartZ=0 EndX=-6.87386 EndY=3 EndZ=0
    g4: LineSegment StartX=-139.417 StartY=-3 StartZ=0 EndX=-6.87386 EndY=-3 EndZ=0
  constraints (15):
    c: Coincident(g1,g0)
    c: Horizontal(g3)
    c: Horizontal(g4)
    c: Coincident(g1,g4)
    c: Coincident(g1,g3)
    c: Coincident(g2,g3)
    c: Coincident(g2,g4)
    c: Symmetric(g1,g1,g-1)
    c: Distance(g1,g1) = 6
    c: Diameter(g0) = 16
    c: Diameter(g1) = 22
    c: DistanceX(g0,g-1) = 150
    c: Equal(g2,g-3)
    c: PointOnObject(g2,g-3)
    c: Equal(g4,g3)
FEATURE [PartDesign::Pad] Pad008
  BaseFeature = -> Pad007
  Direction = (0,0,-1)
  Length = 10
  Length2 = 10
  Profile = -> Sketch017
  ReferenceAxis = -> Sketch017 [N_Axis]
  Refine = true
  Reversed = true
  Type = 0
FEATURE [PartDesign::Plane] DatumPlane001
  AttachmentOffset = pos=(0,0,-145) rot=(0,0,1;0rad)
  Length = 62.49
  MapMode = 5
  Placement = pos=(-130,0,0) rot=(0.57735,0.57735,0.57735;2.0944rad)
  ResizeMode = 0
  Support = -> [Pad008]
  Width = 90.49
FEATURE [Sketcher::SketchObject] Sketch018
  ExternalGeometry = -> [Pad008]
  FullyConstrained = true
  MapMode = 5
  Placement = pos=(-130,0,0) rot=(0.57735,0.57735,0.57735;2.0944rad)
  Support = -> [DatumPlane001]
  sketch-geometry (5):
    g0: Circle CenterX=-1.2e-15 CenterY=32 CenterZ=0 NormalX=0 NormalY=0 NormalZ=1 AngleXU=0 Radius=8
    g1: ArcOfCircle CenterX=-1.2e-15 CenterY=32 CenterZ=0 NormalX=0 NormalY=0 NormalZ=1 AngleXU=0 Radius=11 StartAngle=4.98862 EndAngle=10.7193
    g2: LineSegment StartX=-3 StartY=10 StartZ=0 EndX=-3 EndY=21.417 EndZ=0
    g3: LineSegment StartX=3 StartY=10 StartZ=0 EndX=3 EndY=21.417 EndZ=0
    g4: LineSegment StartX=-3 StartY=10 StartZ=0 EndX=3 EndY=10 EndZ=0
  constraints (12):
    c: Coincident(g0,g-3)
    c: Coincident(g1,g0)
    c: Diameter(g0) = 16
    c: Diameter(g1) = 22
    c: Vertical(g3)
    c: Vertical(g2)
    c: Coincident(g1,g2)
    c: Coincident(g1,g3)
    c: Symmetric(g2,g3,g-2)
    c: Coincident(g4,g2)
    c: Coincident(g4,g3)
    c: Coincident(g2,g-4)
FEATURE [PartDesign::Pad] Pad009
  BaseFeature = -> Pad008
  Direction = (1,0,0)
  Length = 5
  Length2 = 10
  Profile = -> Sketch018
  ReferenceAxis = -> Sketch018 [N_Axis]
  Refine = true
  Type = 0
FEATURE [PartDesign::Body] Body001  label="arm1-skel"
  Group = -> [Sketch010,Pad005,Sketch011,Pad006,Sketch012,Hole002,Sketch013,Pad007,Sketch017,Pad008,DatumPlane001,Sketch018,Pad009]
  Origin = -> Origin002
  Tip = -> Pad009
FEATURE [PartDesign::Chamfer] Chamfer
  Angle = 15
  Base = -> Pad004
  BaseFeature = -> Pad004
  ChamferType = 2
  FlipDirection = true
  Refine = true
  Size = 1
  Size2 = 1
  SupportTransform = false
  UseAllEdges = false
FEATURE [PartDesign::Chamfer] Chamfer001
  Angle = 15
  Base = -> Chamfer [Edge18]
  BaseFeature = -> Chamfer
  ChamferType = 2
  FlipDirection = true
  Refine = true
  Size = 5
  Size2 = 1
  SupportTransform = false
  UseAllEdges = false
FEATURE [PartDesign::Chamfer] Chamfer002
  Angle = 15
  Base = -> Chamfer001 [Edge99]
  BaseFeature = -> Chamfer001
  ChamferType = 2
  FlipDirection = false
  Refine = true
  Size = 1
  Size2 = 1
  SupportTransform = false
  UseAllEdges = false
FEATURE [PartDesign::Chamfer] Chamfer003
  Angle = 15
  Base = -> Chamfer002 [Edge39]
  BaseFeature = -> Chamfer002
  ChamferType = 2
  FlipDirection = true
  Refine = true
  Size = 3
  Size2 = 1
  SupportTransform = false
  UseAllEdges = false
FEATURE [PartDesign::Chamfer] Chamfer004
  Angle = 15
  Base = -> Chamfer003 [Edge79]
  BaseFeature = -> Chamfer003
  ChamferType = 2
  FlipDirection = false
  Refine = true
  Size = 1
  Size2 = 1
  SupportTransform = false
  UseAllEdges = false
FEATURE [PartDesign::Chamfer] Chamfer005
  Angle = 15
  Base = -> Chamfer004 [Edge35,Edge87]
  BaseFeature = -> Chamfer004
  ChamferType = 2
  FlipDirection = true
  Refine = true
  Size = 1
  Size2 = 1
  SupportTransform = false
  UseAllEdges = false
FEATURE [PartDesign::Chamfer] Chamfer006
  Angle = 45
  Base = -> Chamfer005 [Edge5,Edge29]
  BaseFeature = -> Chamfer005
  ChamferType = 0
  FlipDirection = false
  Refine = true
  Size = 7
  Size2 = 1
  SupportTransform = false
  UseAllEdges = false
FEATURE [PartDesign::Plane] DatumPlane002
  Length = 62.49
  MapMode = 5
  Placement = pos=(-125,0,0) rot=(0.57735,0.57735,0.57735;2.0944rad)
  ResizeMode = 0
  Support = -> [Chamfer006]
  Width = 90.49
FEATURE [Sketcher::SketchObject] Sketch019
  ExternalGeometry = -> [Chamfer006]
  FullyConstrained = true
  MapMode = 5
  Placement = pos=(-125,0,0) rot=(0.57735,0.57735,0.57735;2.0944rad)
  Support = -> [DatumPlane002]
  sketch-geometry (4):
    g0: ArcOfCircle CenterX=-1.2e-15 CenterY=32 CenterZ=0 NormalX=0 NormalY=0 NormalZ=1 AngleXU=0 Radius=11 StartAngle=3.39743 EndAngle=6.02735
    g1: LineSegment StartX=-10.642 StartY=29.2164 StartZ=0 EndX=-3 EndY=0 EndZ=0
    g2: LineSegment StartX=-3 StartY=0 StartZ=0 EndX=3 EndY=0 EndZ=0
    g3: LineSegment StartX=3 StartY=0 StartZ=0 EndX=10.642 EndY=29.2164 EndZ=0
  constraints (9):
    c: Coincident(g0,g-3)
    c: PointOnObject(g-3,g0)
    c: PointOnObject(g1,g-1)
    c: Coincident(g1,g2)
    c: Coincident(g2,g3)
    c: Tangent(g0,g1) = -1.5708
    c: Tangent(g0,g3) = -1.5708
    c: Distance(g2,g2) = 6
    c: Symmetric(g1,g2,g-2)
FEATURE [PartDesign::Pad] Pad010
  BaseFeature = -> Chamfer006
  Direction = (1,0,0)
  Length = 10
  Length2 = 10
  Profile = -> Sketch019
  ReferenceAxis = -> Sketch019 [N_Axis]
  Refine = true
  Reversed = true
  Type = 3
  UpToFace = -> Chamfer006 [Face1]
FEATURE [PartDesign::Plane] DatumPlane003
  Length = 62.49
  MapMode = 5
  Placement = pos=(15,0,0) rot=(0.57735,0.57735,0.57735;2.0944rad)
  ResizeMode = 0
  Support = -> [Pad010]
  Width = 90.49
FEATURE [Sketcher::SketchObject] Sketch020
  ExternalGeometry = -> [Pad010]
  FullyConstrained = true
  MapMode = 5
  Placement = pos=(15,0,0) rot=(0.57735,0.57735,0.57735;2.0944rad)
  Support = -> [DatumPlane003]
  sketch-geometry (4):
    g0: ArcOfCircle CenterX=0 CenterY=47 CenterZ=0 NormalX=0 NormalY=0 NormalZ=1 AngleXU=0 Radius=2 StartAngle=0.664501 EndAngle=2.47709
    g1: ArcOfCircle CenterX=-1.2e-15 CenterY=32 CenterZ=0 NormalX=0 NormalY=0 NormalZ=1 AngleXU=0 Radius=11.25 StartAngle=0.664501 EndAngle=2.47709
    g2: LineSegment StartX=-8.85627 StartY=38.9375 StartZ=0 EndX=-1.57445 EndY=48.2333 EndZ=0
    g3: LineSegment StartX=8.85627 StartY=38.9375 StartZ=0 EndX=1.57445 EndY=48.2333 EndZ=0
  constraints (11):
    c: PointOnObject(g0,g-2)
    c: Coincident(g1,g-3)
    c: PointOnObject(g1,g-3)
    c: Horizontal(g1,g1)
    c: Tangent(g2,g1) = 1.5708
    c: Coincident(g3,g1)
    c: Equal(g3,g2)
    c: Coincident(g0,g2)
    c: Tangent(g0,g3) = -1.5708
    c: DistanceY(g1,g0) = 15
    c: Radius(g0) = 2
FEATURE [PartDesign::Pocket] Pocket002
  BaseFeature = -> Pad010
  Direction = (-1,0,0)
  Length = 5
  Length2 = 5
  Profile = -> Sketch020
  ReferenceAxis = -> Sketch020 [N_Axis]
  Refine = true
  Type = 0
FEATURE [PartDesign::Chamfer] Chamfer007
  Angle = 45
  Base = -> Pocket002 [Edge18,Edge6]
  BaseFeature = -> Pocket002
  ChamferType = 0
  FlipDirection = false
  Refine = true
  Size = 2
  Size2 = 1
  SupportTransform = false
  UseAllEdges = false
FEATURE [PartDesign::Fillet] Fillet
  Base = -> Chamfer007 [Edge65,Edge142,Edge84,Edge143]
  BaseFeature = -> Chamfer007
  Radius = 6
  Refine = true
  SupportTransform = false
  UseAllEdges = false
FEATURE [PartDesign::Body] Body  label="arm1s"
  Group = -> [Sketch,Pad,Sketch001,Pad001,Sketch003,Hole,Sketch004,Pad002,Sketch005,Pocket,Sketch006,Hole001,Sketch007,Pocket001,Sketch008,Pad003,DatumPlane,Sketch009,Pad004,Chamfer,Chamfer001,Chamfer002,Chamfer003,Chamfer004,Chamfer005,Chamfer006,DatumPlane002,Sketch019,Pad010,DatumPlane003,Sketch020,Pocket002,Chamfer007,Fillet]
  Origin = -> Origin001
  Tip = -> Fillet
FEATURE [App::Part] Part  label="arm1"
  Group = -> [Body001,Body]
  Origin = -> Origin
COMPONENT P2 — recipe-attached ("arm2", a linked part whose construction recipe lives in a companion FreeCAD document of the same project; that document's serialized recipe follows).
Construction recipe (the companion document, serialized — sketch geometry with constraints, then the solid features built on it; lengths are millimeters unless a unit is written):

FCSTD DOCUMENT  (FreeCAD 2024.1R35694 (Git))
Label: arm2
License: All rights reserved
LicenseURL: https://en.wikipedia.org/wiki/All_rights_reserved
objects: Sketcher::SketchObject×3, PartDesign::Pad×2, PartDesign::Body×2, PartDesign::Chamfer×1, PartDesign::Pocket×1, App::Part×1
note: 13 computed .brp shape members not serialized (recipe doc carries the construction recipe); baked Part::Feature solids carry a one-line shape summary decoded from their .brp

FEATURE [Sketcher::SketchObject] Sketch
  FullyConstrained = true
  MapMode = 5
  Support = -> [XY_Plane001]
  sketch-geometry (9):
    g0: ArcOfCircle CenterX=0 CenterY=0 CenterZ=0 NormalX=0 NormalY=0 NormalZ=1 AngleXU=0 Radius=2.5 StartAngle=2.2143 EndAngle=4.06889
    g1: ArcOfCircle CenterX=0 CenterY=0 CenterZ=0 NormalX=0 NormalY=0 NormalZ=1 AngleXU=0 Radius=4 StartAngle=0.523599 EndAngle=5.75959
    g2: LineSegment StartX=3.4641 StartY=2 StartZ=0 EndX=118 EndY=2 EndZ=0
    g3: LineSegment StartX=118 StartY=2 StartZ=0 EndX=120 EndY=0 EndZ=0
    g4: LineSegment StartX=120 StartY=0 StartZ=0 EndX=118 EndY=-2 EndZ=0
    g5: LineSegment StartX=118 StartY=-2 StartZ=0 EndX=3.4641 EndY=-2 EndZ=0
    g6: LineSegment StartX=-1.5 StartY=2 StartZ=0 EndX=1.5 EndY=2 EndZ=0
    g7: LineSegment StartX=-1.5 StartY=-2 StartZ=0 EndX=1.5 EndY=-2 EndZ=0
    g8: ArcOfCircle CenterX=0 CenterY=0 CenterZ=0 NormalX=0 NormalY=0 NormalZ=1 AngleXU=0 Radius=2.5 StartAngle=5.35589 EndAngle=7.21048
  constraints (26):
    c: Coincident(g0,g-1)
    c: Coincident(g1,g0)
    c: Horizontal(g2)
    c: Coincident(g2,g3)
    c: PointOnObject(g3,g-1)
    c: Coincident(g3,g4)
    c: Coincident(g4,g5)
    c: Horizontal(g6)
    c: Horizontal(g7)
    c: Equal(g6,g7)
    c: Coincident(g0,g6)
    c: Equal(g0,g8)
    c: Coincident(g0,g7)
    c: Coincident(g8,g7)
    c: Coincident(g0,g8)
    c: Diameter(g8) = 5
    c: DistanceY(g7,g6) = 4
    c: Symmetric(g4,g2,g-1)
    c: Angle(g3,g4) = 1.5708
    c: Distance(g2,g4) = 4
    c: Coincident(g1,g5)
    c: Diameter(g1) = 8
    c: DistanceX(g-1,g3) = 120
    c: Coincident(g1,g2)
    c: Equal(g5,g2)
    c: Coincident(g6,g8)
FEATURE [PartDesign::Pad] Pad
  Direction = (0,0,1)
  Length = 5
  Length2 = 10
  Profile = -> Sketch
  ReferenceAxis = -> Sketch [N_Axis]
  Refine = true
  Type = 0
FEATURE [PartDesign::Body] Body  label="arm2-skel"
  Group = -> [Sketch,Pad]
  Origin = -> Origin001
  Tip = -> Pad
FEATURE [Sketcher::SketchObject] Sketch001
  FullyConstrained = true
  MapMode = 5
  Support = -> [XY_Plane002]
  sketch-geometry (9):
    g0: ArcOfCircle CenterX=0 CenterY=0 CenterZ=0 NormalX=0 NormalY=0 NormalZ=1 AngleXU=0 Radius=2.5 StartAngle=2.2143 EndAngle=4.06889
    g1: ArcOfCircle CenterX=0 CenterY=0 CenterZ=0 NormalX=0 NormalY=0 NormalZ=1 AngleXU=0 Radius=4 StartAngle=0.523599 EndAngle=5.75959
    g2: LineSegment StartX=3.4641 StartY=2 StartZ=0 EndX=118 EndY=2 EndZ=0
    g3: LineSegment StartX=118 StartY=2 StartZ=0 EndX=120 EndY=0 EndZ=0
    g4: LineSegment StartX=120 StartY=0 StartZ=0 EndX=118 EndY=-2 EndZ=0
    g5: LineSegment StartX=118 StartY=-2 StartZ=0 EndX=3.4641 EndY=-2 EndZ=0
    g6: LineSegment StartX=-1.5 StartY=2 StartZ=0 EndX=1.5 EndY=2 EndZ=0
    g7: LineSegment StartX=-1.5 StartY=-2 StartZ=0 EndX=1.5 EndY=-2 EndZ=0
    g8: ArcOfCircle CenterX=0 CenterY=0 CenterZ=0 NormalX=0 NormalY=0 NormalZ=1 AngleXU=0 Radius=2.5 StartAngle=5.35589 EndAngle=7.21048
  constraints (26):
    c: Coincident(g0,g-1)
    c: Coincident(g1,g0)
    c: Horizontal(g2)
    c: Coincident(g2,g3)
    c: PointOnObject(g3,g-1)
    c: Coincident(g3,g4)
    c: Coincident(g4,g5)
    c: Horizontal(g6)
    c: Horizontal(g7)
    c: Equal(g6,g7)
    c: Coincident(g0,g6)
    c: Equal(g0,g8)
    c: Coincident(g0,g7)
    c: Coincident(g8,g7)
    c: Coincident(g0,g8)
    c: Diameter(g8) = 5
    c: DistanceY(g7,g6) = 4
    c: Symmetric(g4,g2,g-1)
    c: Angle(g3,g4) = 1.5708
    c: Distance(g2,g4) = 4
    c: Coincident(g1,g5)
    c: Diameter(g1) = 8
    c: DistanceX(g-1,g3) = 120
    c: Coincident(g1,g2)
    c: Equal(g5,g2)
    c: Coincident(g6,g8)
FEATURE [PartDesign::Pad] Pad001
  Direction = (0,0,1)
  Length = 5
  Length2 = 10
  Profile = -> Sketch001
  ReferenceAxis = -> Sketch001 [N_Axis]
  Refine = true
  Type = 0
FEATURE [PartDesign::Chamfer] Chamfer
  Angle = 15
  Base = -> Pad001 [Edge24,Edge21,Edge18,Edge26,Edge25,Edge27,Edge19,Edge22]
  BaseFeature = -> Pad001
  ChamferType = 2
  FlipDirection = false
  Refine = true
  Size = 1
  Size2 = 1
  SupportTransform = false
  UseAllEdges = false
FEATURE [Sketcher::SketchObject] Sketch002
  ExternalGeometry = -> [Chamfer]
  FullyConstrained = true
  MapMode = 5
  Placement = pos=(0,0,5) rot=(0,0,1;0rad)
  Support = -> [Chamfer]
  sketch-geometry (4):
    g0: LineSegment StartX=3.4641 StartY=-2 StartZ=0 EndX=203.464 EndY=-2 EndZ=0
    g1: LineSegment StartX=203.464 StartY=-2 StartZ=0 EndX=203.464 EndY=2 EndZ=0
    g2: LineSegment StartX=203.464 StartY=2 StartZ=0 EndX=3.4641 EndY=2 EndZ=0
    g3: ArcOfCircle CenterX=0 CenterY=0 CenterZ=0 NormalX=0 NormalY=0 NormalZ=1 AngleXU=0 Radius=4 StartAngle=5.75959 EndAngle=6.80678
  constraints (11):
    c: Coincident(g0,g1)
    c: Coincident(g1,g2)
    c: Vertical(g1)
    c: Horizontal(g0)
    c: Horizontal(g2)
    c: Coincident(g3,g-3)
    c: Coincident(g2,g-3)
    c: Coincident(g0,g-3)
    c: DistanceX(g2,g2) = 200
    c: Coincident(g3,g2)
    c: PointOnObject(g3,g0)
FEATURE [PartDesign::Pocket] Pocket
  BaseFeature = -> Chamfer
  Direction = (0,0,-1)
  Length = 1
  Length2 = 5
  Profile = -> Sketch002
  ReferenceAxis = -> Sketch002 [N_Axis]
  Refine = true
  Type = 0
FEATURE [PartDesign::Body] Body001  label="arm2s"
  Group = -> [Sketch001,Pad001,Chamfer,Sketch002,Pocket]
  Origin = -> Origin002
  Tip = -> Pocket
FEATURE [App::Part] Part  label="arm2"
  Group = -> [Body,Body001]
  Origin = -> Origin
PROVENANCE & LICENSES
A FreeCAD (.FCStd) document from a public repository crawl; recipes are the document's own serialized feature recipes (and, for linked parts, companion documents' recipes).
License: lgpl-3.0.
